# Revit family: hansgrohe_01001180-uBox-universal-Base-set-for-lin
name_source: partatom
category: Generic Models
revit_build: Autodesk Revit 2018 (Build: 20170223_1515(x64)
units: mm (PartAtom-declared; Revit-internal decimal feet)

## family parameters
Always vertical = No
Can host rebar = No
Cut with Voids When Loaded = No
Part Type = Normal
Room Calculation Point = No
Round Connector Dimension = Use Diameter
Shared = No
Work Plane-Based = No

## types (1)
- Default
    Brand url = http://www.hansgrohe-int.com
    Design country = Germany
    Edition number = 1
    GTIN code = https://4059625350850
    IFC Classification = Sanitary Terminal
    Installation instructions = https://www.hansgrohe.com
    Manufacturer country = Germany
    Manufacturer name = hansgrohe
    Materia = Hansgrohe - Paket Wright - Default
    Material main = Plastic
    Product Guid = 2161642f-c8ba-408b-ab0a-2ac3bddedd11
    Product SKU = 01001180
    Product data url = https://bimobject.com
    Product family = uBox universal
    Product group = Concealed basic set shower drains
    Product name = 01001180 uBox universal Base set for linear shower drains for standard installation
    Product url = https://www.hansgrohe.com
    QR code = http://bimobject.com
    Technical description = https://www.hansgrohe.com

## geometry (parser evidence)
native form markers: Sweep x3
no freeform markers — native parametric forms only
